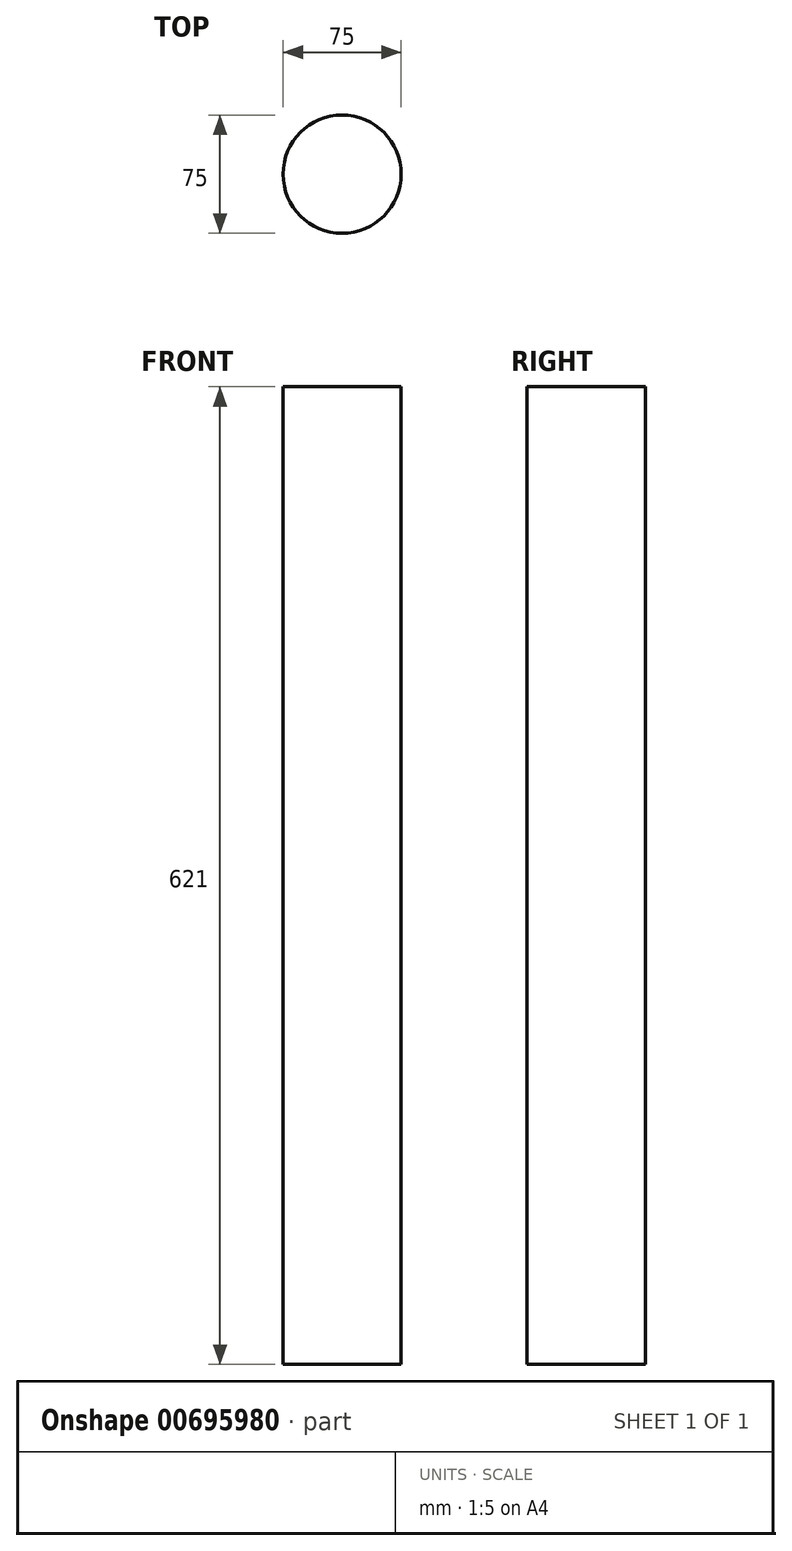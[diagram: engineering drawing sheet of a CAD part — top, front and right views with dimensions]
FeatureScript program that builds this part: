
annotation { "Feature Type Name" : "Feature", "Feature Type Description" : "" }
export const myFeature = defineFeature(function(context is Context, id is Id, definition is map)
    precondition{}
    {
        {
            var Q0;
            Q0=qCreatedBy(makeId("Top.planeOp"),FACE);
            var sketch = newSketch(context, id + "F0", { "sketchPlane" : qUnion([Q0])});
            skCircle(sketch, "E0", {"center": v(0, 0) * mm, "radius": 37.5 * mm});
            skSolve(sketch);
        }
        {
            var Q0;
            Q0 = qSketchRegion(id + "F0", true);
            extrude(context, id + "F1", {"entities" : qUnion([Q0]), "depth" : 621 * mm, "offsetDistance" : 25.4 * mm});
        }
    });
